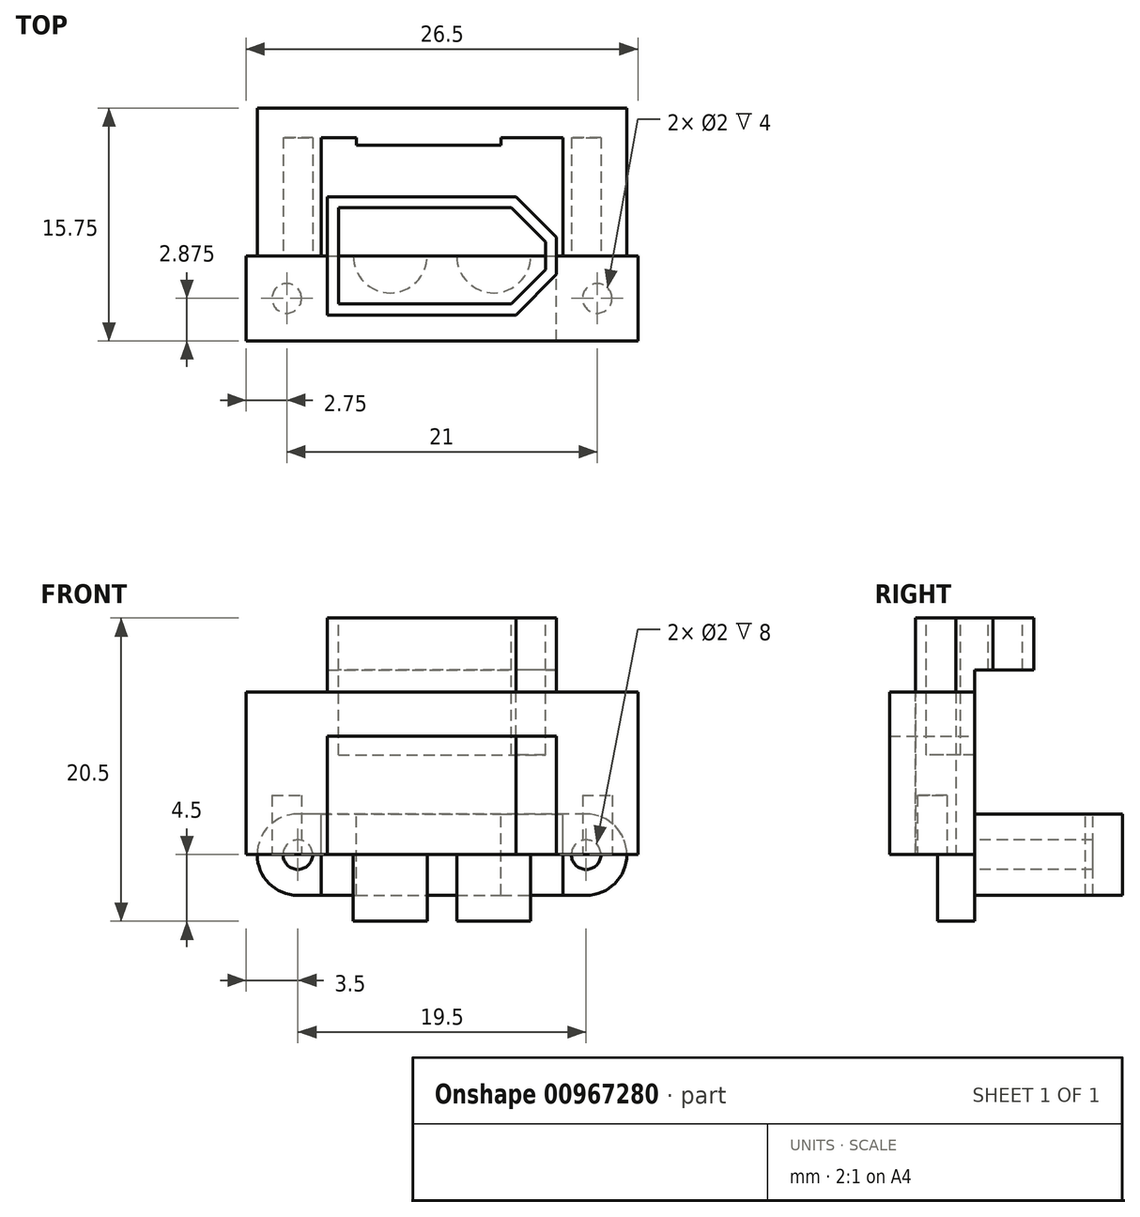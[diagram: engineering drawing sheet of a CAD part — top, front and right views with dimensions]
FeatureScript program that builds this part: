
annotation { "Feature Type Name" : "Feature", "Feature Type Description" : "" }
export const myFeature = defineFeature(function(context is Context, id is Id, definition is map)
    precondition{}
    {
        {
            var Q0;
            Q0=qCreatedBy(makeId("Top.planeOp"),FACE);
            var sketch = newSketch(context, id + "F0", { "sketchPlane" : qUnion([Q0])});
            skLineSegment(sketch, "E0.bottom", {"start": v(-7.75, 4) * mm, "end": v(7.75, 4) * mm});
            skLineSegment(sketch, "E0.top", {"start": v(-7.75, -4) * mm, "end": v(7.75, -4) * mm});
            skLineSegment(sketch, "E0.left", {"start": v(-7.75, 4) * mm, "end": v(-7.75, -4) * mm});
            skLineSegment(sketch, "E0.right", {"start": v(7.75, 4) * mm, "end": v(7.75, -4) * mm});
            skSolve(sketch);
        }
        {
            var Q0;
            Q0=makeQuery(id+"F0.imprint","IMPRINT",FACE,{"disambiguationData":[TD([[makeQuery(id+"F0.imprint","IMPRINT",EDGE,{"derivedFrom":sQuery(id+"F0.wireOp",EDGE,"E0.bottom")}),-1.0]])]});
            extrude(context, id + "F1", {"entities" : qUnion([Q0]), "depth" : 16 * mm});
        }
        {
            var Q0;
            Q0=makeQuery(id+"F1.opExtrude","SWEPT_EDGE",EDGE,{"disambiguationData":[OSD([sQuery(id+"F0.wireOp",EDGE,"E0.top"),sQuery(id+"F0.wireOp",EDGE,"E0.right")])]});
            var Q1;
            Q1=makeQuery(id+"F1.opExtrude","SWEPT_EDGE",EDGE,{"disambiguationData":[OSD([sQuery(id+"F0.wireOp",EDGE,"E0.bottom"),sQuery(id+"F0.wireOp",EDGE,"E0.right")])]});
            chamfer(context, id + "F2", {"entities" : qUnion([Q0, Q1]), "width" : 2.75 * mm, "tangentPropagation" : true});
        }
        {
            var Q0;
            Q0=makeQuery(id+"F1.opExtrude","CAP_FACE",FACE,{"disambiguationData":[OSD([sQuery(id+"F0.wireOp",EDGE,"E0.bottom"),sQuery(id+"F0.wireOp",EDGE,"E0.top"),sQuery(id+"F0.wireOp",EDGE,"E0.left"),sQuery(id+"F0.wireOp",EDGE,"E0.right")])],"isStart":false});
            var sketch = newSketch(context, id + "F3", { "sketchPlane" : qUnion([Q0])});
            skLineSegment(sketch, "E1.bottom", {"start": v(-7, 3.25) * mm, "end": v(4.69, 3.25) * mm});
            skLineSegment(sketch, "E1.top", {"start": v(-7, -3.25) * mm, "end": v(4.69, -3.25) * mm});
            skLineSegment(sketch, "E1.left", {"start": v(-7, 3.25) * mm, "end": v(-7, -3.25) * mm});
            skLineSegment(sketch, "E2", {"start": v(4.69, 3.25) * mm, "end": v(7, 0.94) * mm});
            skLineSegment(sketch, "E3", {"start": v(7, 0.94) * mm, "end": v(7, -0.94) * mm});
            skLineSegment(sketch, "E4", {"start": v(7, -0.94) * mm, "end": v(4.69, -3.25) * mm});
            skSolve(sketch);
        }
        {
            var Q0;
            Q0=qSketchRegion(id+"F3",true);
            extrude(context, id + "F4", {"entities" : qUnion([Q0]), "operationType" : NewBodyOperationType.REMOVE, "oppositeDirection" : true, "depth" : 9.25 * mm});
        }
        {
            var Q0;
            Q0=makeQuery(id+"F1.opExtrude","CAP_FACE",FACE,{"disambiguationData":[OSD([sQuery(id+"F0.wireOp",EDGE,"E0.bottom"),sQuery(id+"F0.wireOp",EDGE,"E0.top"),sQuery(id+"F0.wireOp",EDGE,"E0.left"),sQuery(id+"F0.wireOp",EDGE,"E0.right")])],"isStart":true});
            var sketch = newSketch(context, id + "F5", { "sketchPlane" : qUnion([Q0])});
            skCircle(sketch, "E5", {"center": v(-3.5, 0) * mm, "radius": 2.5 * mm});
            skCircle(sketch, "E6", {"center": v(3.5, 0) * mm, "radius": 2.5 * mm});
            skSolve(sketch);
        }
        {
            var Q0;
            Q0=qSketchRegion(id+"F5",true);
            extrude(context, id + "F6", {"entities" : qUnion([Q0]), "operationType" : NewBodyOperationType.ADD, "depth" : 4.5 * mm});
        }
        {
            var Q0;
            Q0=makeQuery(id+"F1.opExtrude","SWEPT_FACE",FACE,{"disambiguationData":[OSD([sQuery(id+"F0.wireOp",EDGE,"E0.bottom")])]});
            var sketch = newSketch(context, id + "F7", { "sketchPlane" : qUnion([Q0])});
            skLineSegment(sketch, "E7.bottom", {"start": v(-3.75, 6.75) * mm, "end": v(6.25, 6.75) * mm});
            skLineSegment(sketch, "E7.top", {"start": v(-3.75, 1) * mm, "end": v(6.25, 1) * mm});
            skLineSegment(sketch, "E7.left", {"start": v(-3.75, 6.75) * mm, "end": v(-3.75, 1) * mm});
            skLineSegment(sketch, "E7.right", {"start": v(6.25, 6.75) * mm, "end": v(6.25, 1) * mm});
            skSolve(sketch);
        }
        {
            var Q0;
            Q0=makeQuery(id+"F7.imprint","IMPRINT",FACE,{"disambiguationData":[TD([[makeQuery(id+"F7.imprint","IMPRINT",EDGE,{"derivedFrom":sQuery(id+"F7.wireOp",EDGE,"E7.bottom")}),-1.0]])]});
            extrude(context, id + "F8", {"entities" : qUnion([Q0]), "operationType" : NewBodyOperationType.REMOVE, "oppositeDirection" : true, "depth" : 0.5 * mm});
        }
        {
            var Q0;
            Q0=qCreatedBy(makeId("Front.planeOp"),FACE);
            var sketch = newSketch(context, id + "F9", { "sketchPlane" : qUnion([Q0])});
            skLineSegment(sketch, "E8.top", {"start": v(-7.75, 8) * mm, "end": v(7.75, 8) * mm});
            skLineSegment(sketch, "E8.left", {"start": v(-7.75, 0) * mm, "end": v(-7.75, 8) * mm});
            skLineSegment(sketch, "E8.right", {"start": v(7.75, 0) * mm, "end": v(7.75, 8) * mm});
            skLineSegment(sketch, "E9.bottom", {"start": v(-13.25, 0) * mm, "end": v(-7.75, 0) * mm});
            skLineSegment(sketch, "E9.top", {"start": v(-13.25, 11) * mm, "end": v(13.25, 11) * mm});
            skLineSegment(sketch, "E9.left", {"start": v(-13.25, 0) * mm, "end": v(-13.25, 11) * mm});
            skLineSegment(sketch, "E9.right", {"start": v(13.25, 0) * mm, "end": v(13.25, 11) * mm});
            skLineSegment(sketch, "E10.trimOffspring", {"start": v(7.75, 0) * mm, "end": v(13.25, 0) * mm});
            skSolve(sketch);
        }
        {
            var Q0;
            Q0=qSketchRegion(id+"F9",true);
            extrude(context, id + "F10", {"entities" : qUnion([Q0]), "depth" : 5.75 * mm});
        }
        {
            var Q0;
            Q0=makeQuery(id+"F10.opExtrude","SWEPT_FACE",FACE,{"disambiguationData":[OSD([sQuery(id+"F9.wireOp",EDGE,"E9.bottom")])]});
            var sketch = newSketch(context, id + "F11", { "sketchPlane" : qUnion([Q0])});
            skCircle(sketch, "E11", {"center": v(-10.5, 2.88) * mm, "radius": 1 * mm});
            skCircle(sketch, "E12", {"center": v(10.5, 2.88) * mm, "radius": 1 * mm});
            skSolve(sketch);
        }
        {
            var Q0;
            Q0=qSketchRegion(id+"F11",true);
            extrude(context, id + "F12", {"entities" : qUnion([Q0]), "operationType" : NewBodyOperationType.REMOVE, "oppositeDirection" : true, "depth" : 4 * mm});
        }
        {
            var Q0;
            Q0=qCreatedBy(makeId("Front.planeOp"),FACE);
            var sketch = newSketch(context, id + "F13", { "sketchPlane" : qUnion([Q0])});
            skArc(sketch, "E13", {"start": v(9.75, -2.75) * mm, "mid": v(12.5, 0) * mm, "end": v(9.75, 2.75) * mm});
            skArc(sketch, "E14", {"start": v(-9.75, 2.75) * mm, "mid": v(-12.5, 0) * mm, "end": v(-9.75, -2.75) * mm});
            skLineSegment(sketch, "E15.bottom", {"start": v(9.75, 2.75) * mm, "end": v(-9.75, 2.75) * mm});
            skLineSegment(sketch, "E15.top", {"start": v(9.75, -2.75) * mm, "end": v(-9.75, -2.75) * mm});
            skSolve(sketch);
        }
        {
            var Q0;
            Q0=qSketchRegion(id+"F13",true);
            extrude(context, id + "F14", {"entities" : qUnion([Q0]), "oppositeDirection" : true, "depth" : 10 * mm});
        }
        {
            var Q0;
            Q0=qCreatedBy(makeId("Top.planeOp"),FACE);
            var sketch = newSketch(context, id + "F15", { "sketchPlane" : qUnion([Q0])});
            skLineSegment(sketch, "E16.bottom", {"start": v(-8.18, 0) * mm, "end": v(8.18, 0) * mm});
            skLineSegment(sketch, "E16.top", {"start": v(-8.18, 8) * mm, "end": v(-5.78, 8) * mm});
            skLineSegment(sketch, "E16.left", {"start": v(-8.18, 0) * mm, "end": v(-8.18, 8) * mm});
            skLineSegment(sketch, "E16.right", {"start": v(8.18, 0) * mm, "end": v(8.18, 8) * mm});
            skLineSegment(sketch, "E17.top", {"start": v(-5.78, 7.5) * mm, "end": v(3.98, 7.5) * mm});
            skLineSegment(sketch, "E17.left", {"start": v(-5.78, 8) * mm, "end": v(-5.78, 7.5) * mm});
            skLineSegment(sketch, "E17.right", {"start": v(3.98, 8) * mm, "end": v(3.98, 7.5) * mm});
            skLineSegment(sketch, "E18.trimOffspring", {"start": v(3.98, 8) * mm, "end": v(8.18, 8) * mm});
            skSolve(sketch);
        }
        {
            var Q0;
            Q0=qSketchRegion(id+"F15",true);
            extrude(context, id + "F16", {"entities" : qUnion([Q0]), "operationType" : NewBodyOperationType.REMOVE, "endBound" : BoundingType.SYMMETRIC, "oppositeDirection" : true, "depth" : 25 * mm});
        }
        {
            var Q0;
            {var subQ0=sQuery(id+"F13.wireOp",EDGE,"E14");var subQ1=sQuery(id+"F13.wireOp",EDGE,"E15.bottom");var subQ2=sQuery(id+"F13.wireOp",EDGE,"E15.top");Q0=makeQuery(id+"F16.boolean.opBoolean","SPLIT",FACE,{"disambiguationData":[TD([makeQuery(id+"F14.opExtrude","SWEPT_FACE",FACE,{"disambiguationData":[OSD([subQ0])]})])],"derivedFrom":makeQuery(id+"F14.opExtrude","CAP_FACE",FACE,{"disambiguationData":[OSD([sQuery(id+"F13.wireOp",EDGE,"E13"),subQ0,subQ1,subQ2])],"isStart":true})});}
            var sketch = newSketch(context, id + "F17", { "sketchPlane" : qUnion([Q0])});
            skCircle(sketch, "E19", {"center": v(-9.75, 0) * mm, "radius": 1 * mm});
            skCircle(sketch, "E20", {"center": v(9.75, 0) * mm, "radius": 1 * mm});
            skSolve(sketch);
        }
        {
            var Q0;
            Q0=qSketchRegion(id+"F17",true);
            extrude(context, id + "F18", {"entities" : qUnion([Q0]), "operationType" : NewBodyOperationType.REMOVE, "oppositeDirection" : true, "depth" : 8 * mm});
        }
    });
